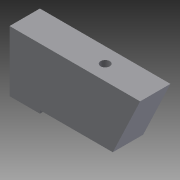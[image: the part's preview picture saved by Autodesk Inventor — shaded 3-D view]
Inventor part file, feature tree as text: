
AUTODESK INVENTOR PART (.ipt)
format: ipt  version: 2015 (Build 190159000, 159)  size: 82,944 bytes
history: native  units: mm
features: extrude x2, sketch x2
ambient origin geometry x8: Origin, YZ Plane, XZ Plane, XY Plane, X Axis, Y Axis, Z Axis, Center Point
bodies: Solid1 (feature_tree)
feature tree (4):
  extrude  "Extrusion1"  Depth=10.0mm
  extrude  "Extrusion2"  Depth=19.0mm
  sketch  "Sketch1"  dims[d0=43.0mm d2=10.0mm]
  sketch  "Sketch2"  dims[d3=1.0mm d4=24.0mm d5=10.0mm d6=0.0mm d7=26.5mm d8=3.0mm d9=19.0mm d10=0.0mm]
